# Revit family: Accessory-Teknion-JNABA-Beam_Mounted_Accessories-R2018
name_source: partatom
category: Furniture
revit_build: Autodesk Revit 2018 (Build: 20190510_1515(x64)
units: mm (PartAtom-declared; Revit-internal decimal feet)

## family parameters
Always vertical = Yes
Cut with Voids When Loaded = No
OmniClass Number = 23.40.20.00
OmniClass Title = General Furniture and Specialties
Room Calculation Point = No
Shared = Yes
Work Plane-Based = No

## types (4) — shared parameters
Assembly Code = E2020200
Manufacturer = Teknion
Manufacturer Fax = 416.661.4586
Part Number = JNABA
Product Documentation Link = http://www.teknion.com
Product Line = Expansion Cityline
Product Page URL = http://www.teknion.com
Series = Expansion Cityline
Sustainability Data = http://www.teknion.com
URL = www.teknion.com
Unit Weight URL = http://www.teknion.com
Warranty = http://www.teknion.com

## per-type parameters (varying)
| type | Description | Model | Reference Depth B |
| Hook Style | Beam Mounted Accessory, Hook Style | JNABAH_ | 2.5 " |
| Bag Drop Style | Beam Mounted Accessory, Bag Drop Style | JNABAB_ | 6.89 " |
| Side Tray Style | Beam Mounted Accessory, Side Tray Style | JNABAS_ | 4 " |
| Tablet Style | Beam Mounted Accessory, Tablet Style | JNABAT_ | 2.5 " |

type visibility flags: 4 boolean params named "<type name>" — each type sets only its own to Yes (folded from table)

## geometry (parser evidence)
native form markers: Sweep x3
no freeform markers — native parametric forms only
